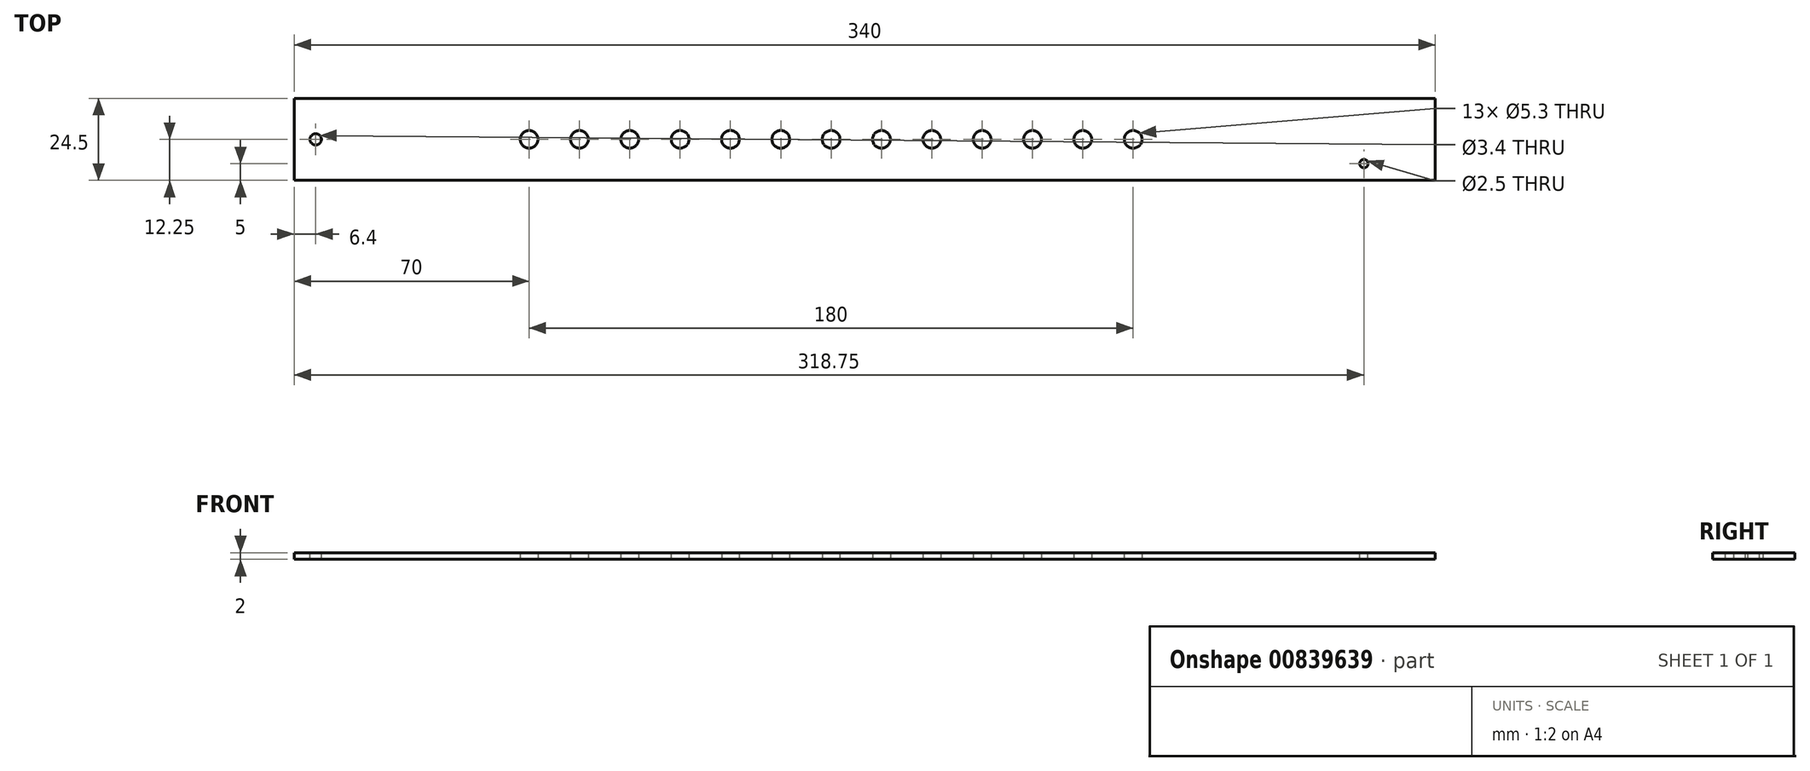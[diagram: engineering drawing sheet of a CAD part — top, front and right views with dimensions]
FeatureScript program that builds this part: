
annotation { "Feature Type Name" : "Feature", "Feature Type Description" : "" }
export const myFeature = defineFeature(function(context is Context, id is Id, definition is map)
    precondition{}
    {
        {
            var Q0;
            Q0=qCreatedBy(makeId("Top.planeOp"),FACE);
            var sketch = newSketch(context, id + "F0", { "sketchPlane" : qUnion([Q0])});
            skLineSegment(sketch, "E0.bottom", {"start": v(150, -12.25) * mm, "end": v(-150, -12.25) * mm});
            skLineSegment(sketch, "E0.top", {"start": v(150, 12.25) * mm, "end": v(-150, 12.25) * mm});
            skLineSegment(sketch, "E0.left", {"start": v(150, -12.25) * mm, "end": v(150, 12.25) * mm});
            skLineSegment(sketch, "E0.right", {"start": v(-150, -12.25) * mm, "end": v(-150, 12.25) * mm});
            skPoint(sketch, "E0.middle", {"position": v(0, 0) * mm});
            skCircle(sketch, "E1.3.0.0", {"center": v(-90, 0) * mm, "radius": 2.65 * mm});
            skCircle(sketch, "E1.4.0.0", {"center": v(-75, 0) * mm, "radius": 2.65 * mm});
            skCircle(sketch, "E1.5.0.0", {"center": v(-60, 0) * mm, "radius": 2.65 * mm});
            skCircle(sketch, "E1.6.0.0", {"center": v(-45, 0) * mm, "radius": 2.65 * mm});
            skCircle(sketch, "E1.7.0.0", {"center": v(-30, 0) * mm, "radius": 2.65 * mm});
            skCircle(sketch, "E1.8.0.0", {"center": v(-15, 0) * mm, "radius": 2.65 * mm});
            skCircle(sketch, "E1.9.0.0", {"center": v(0, 0) * mm, "radius": 2.65 * mm});
            skCircle(sketch, "E1.10.0.0", {"center": v(15, 0) * mm, "radius": 2.65 * mm});
            skCircle(sketch, "E1.11.0.0", {"center": v(30, 0) * mm, "radius": 2.65 * mm});
            skCircle(sketch, "E1.12.0.0", {"center": v(45, 0) * mm, "radius": 2.65 * mm});
            skCircle(sketch, "E1.13.0.0", {"center": v(60, 0) * mm, "radius": 2.65 * mm});
            skCircle(sketch, "E1.14.0.0", {"center": v(75, 0) * mm, "radius": 2.65 * mm});
            skCircle(sketch, "E1.15.0.0", {"center": v(90, 0) * mm, "radius": 2.65 * mm});
            skLineSegment(sketch, "E1.direction1", {"start": v(-135, 0) * mm, "end": v(-120, 0) * mm, "construction": true});
            skSolve(sketch);
        }
        {
            var Q0;
            Q0=makeQuery(id+"F0.imprint","IMPRINT",FACE,{"disambiguationData":[TD([[makeQuery(id+"F0.imprint","IMPRINT",EDGE,{"derivedFrom":sQuery(id+"F0.wireOp",EDGE,"E0.bottom")}),-1.0]])]});
            extrude(context, id + "F1", {"entities" : qUnion([Q0]), "depth" : 2 * mm, "offsetDistance" : 25 * mm});
        }
        {
            var Q0;
            Q0=makeQuery(id+"F1.opExtrude","SWEPT_FACE",FACE,{"disambiguationData":[OSD([sQuery(id+"F0.wireOp",EDGE,"E0.right")])]});
            extrude(context, id + "F2", {"entities" : qUnion([Q0]), "operationType" : NewBodyOperationType.ADD, "depth" : 10 * mm, "offsetDistance" : 25 * mm});
        }
        {
            var Q0;
            Q0=makeQuery(id+"F1.opExtrude","SWEPT_FACE",FACE,{"disambiguationData":[OSD([sQuery(id+"F0.wireOp",EDGE,"E0.left")])]});
            extrude(context, id + "F3", {"entities" : qUnion([Q0]), "operationType" : NewBodyOperationType.ADD, "depth" : 30 * mm, "offsetDistance" : 25 * mm});
        }
        {
            var Q0;
            {var subQ0=sQuery(id+"F0.wireOp",EDGE,"E0.left");var subQ1=sQuery(id+"F0.wireOp",EDGE,"E0.right");Q0=makeQuery(id+"F3.boolean.opBoolean","MERGE",FACE,{"derivedFrom":[makeQuery(id+"F2.boolean.opBoolean","MERGE",FACE,{"derivedFrom":[makeQuery(id+"F1.opExtrude","CAP_FACE",FACE,{"disambiguationData":[OSD([sQuery(id+"F0.wireOp",EDGE,"E0.bottom"),sQuery(id+"F0.wireOp",EDGE,"E0.top"),subQ0,subQ1,sQuery(id+"F0.wireOp",EDGE,"LckrCdrf-Oz9b-iWqB-HkfW-gHpTPrbceAxr"),sQuery(id+"F0.wireOp",EDGE,"E1.1.0.0"),sQuery(id+"F0.wireOp",EDGE,"E1.2.0.0"),sQuery(id+"F0.wireOp",EDGE,"E1.3.0.0"),sQuery(id+"F0.wireOp",EDGE,"E1.4.0.0"),sQuery(id+"F0.wireOp",EDGE,"E1.5.0.0"),sQuery(id+"F0.wireOp",EDGE,"E1.6.0.0"),sQuery(id+"F0.wireOp",EDGE,"E1.7.0.0"),sQuery(id+"F0.wireOp",EDGE,"E1.8.0.0"),sQuery(id+"F0.wireOp",EDGE,"E1.9.0.0"),sQuery(id+"F0.wireOp",EDGE,"E1.10.0.0"),sQuery(id+"F0.wireOp",EDGE,"E1.11.0.0"),sQuery(id+"F0.wireOp",EDGE,"E1.12.0.0"),sQuery(id+"F0.wireOp",EDGE,"E1.13.0.0"),sQuery(id+"F0.wireOp",EDGE,"E1.14.0.0"),sQuery(id+"F0.wireOp",EDGE,"E1.15.0.0"),sQuery(id+"F0.wireOp",EDGE,"E1.16.0.0"),sQuery(id+"F0.wireOp",EDGE,"E1.17.0.0"),sQuery(id+"F0.wireOp",EDGE,"E1.18.0.0")])],"isStart":false}),makeQuery(id+"F2.opExtrude","SWEPT_FACE",FACE,{"disambiguationData":[OSD([subQ1]),TDD([makeQuery(id+"F1.opExtrude","CAP_EDGE",EDGE,{"disambiguationData":[OSD([subQ1])],"isStart":false})])]})]}),makeQuery(id+"F3.opExtrude","SWEPT_FACE",FACE,{"disambiguationData":[OSD([subQ0]),TDD([makeQuery(id+"F1.opExtrude","CAP_EDGE",EDGE,{"disambiguationData":[OSD([subQ0])],"isStart":false})])]})]});}
            var sketch = newSketch(context, id + "F4", { "sketchPlane" : qUnion([Q0])});
            skCircle(sketch, "E2", {"center": v(-153.6, 0) * mm, "radius": 1.7 * mm});
            skSolve(sketch);
        }
        {
            var Q0;
            Q0=makeQuery(id+"F4.imprint","IMPRINT",FACE,{"disambiguationData":[TD([[makeQuery(id+"F4.imprint","IMPRINT",EDGE,{"derivedFrom":sQuery(id+"F4.wireOp",EDGE,"E2")}),1.0]])]});
            extrude(context, id + "F5", {"entities" : qUnion([Q0]), "operationType" : NewBodyOperationType.REMOVE, "endBound" : BoundingType.UP_TO_NEXT, "oppositeDirection" : true, "depth" : 25 * mm, "offsetDistance" : 25 * mm});
        }
        {
            var Q0;
            {var subQ0=sQuery(id+"F0.wireOp",EDGE,"E0.left");var subQ1=sQuery(id+"F0.wireOp",EDGE,"E0.right");Q0=makeQuery(id+"F3.boolean.opBoolean","MERGE",FACE,{"derivedFrom":[makeQuery(id+"F2.boolean.opBoolean","MERGE",FACE,{"derivedFrom":[makeQuery(id+"F1.opExtrude","CAP_FACE",FACE,{"disambiguationData":[OSD([sQuery(id+"F0.wireOp",EDGE,"E0.bottom"),sQuery(id+"F0.wireOp",EDGE,"E0.top"),subQ0,subQ1,sQuery(id+"F0.wireOp",EDGE,"LckrCdrf-Oz9b-iWqB-HkfW-gHpTPrbceAxr"),sQuery(id+"F0.wireOp",EDGE,"E1.1.0.0"),sQuery(id+"F0.wireOp",EDGE,"E1.2.0.0"),sQuery(id+"F0.wireOp",EDGE,"E1.3.0.0"),sQuery(id+"F0.wireOp",EDGE,"E1.4.0.0"),sQuery(id+"F0.wireOp",EDGE,"E1.5.0.0"),sQuery(id+"F0.wireOp",EDGE,"E1.6.0.0"),sQuery(id+"F0.wireOp",EDGE,"E1.7.0.0"),sQuery(id+"F0.wireOp",EDGE,"E1.8.0.0"),sQuery(id+"F0.wireOp",EDGE,"E1.9.0.0"),sQuery(id+"F0.wireOp",EDGE,"E1.10.0.0"),sQuery(id+"F0.wireOp",EDGE,"E1.11.0.0"),sQuery(id+"F0.wireOp",EDGE,"E1.12.0.0"),sQuery(id+"F0.wireOp",EDGE,"E1.13.0.0"),sQuery(id+"F0.wireOp",EDGE,"E1.14.0.0"),sQuery(id+"F0.wireOp",EDGE,"E1.15.0.0"),sQuery(id+"F0.wireOp",EDGE,"E1.16.0.0"),sQuery(id+"F0.wireOp",EDGE,"E1.17.0.0"),sQuery(id+"F0.wireOp",EDGE,"E1.18.0.0")])],"isStart":false}),makeQuery(id+"F2.opExtrude","SWEPT_FACE",FACE,{"disambiguationData":[OSD([subQ1]),TDD([makeQuery(id+"F1.opExtrude","CAP_EDGE",EDGE,{"disambiguationData":[OSD([subQ1])],"isStart":false})])]})]}),makeQuery(id+"F3.opExtrude","SWEPT_FACE",FACE,{"disambiguationData":[OSD([subQ0]),TDD([makeQuery(id+"F1.opExtrude","CAP_EDGE",EDGE,{"disambiguationData":[OSD([subQ0])],"isStart":false})])]})]});}
            var sketch = newSketch(context, id + "F6", { "sketchPlane" : qUnion([Q0])});
            skCircle(sketch, "E3", {"center": v(158.75, -7.25) * mm, "radius": 1.25 * mm});
            skSolve(sketch);
        }
        {
            var Q0;
            Q0=makeQuery(id+"F6.imprint","IMPRINT",FACE,{"disambiguationData":[TD([[makeQuery(id+"F6.imprint","IMPRINT",EDGE,{"derivedFrom":sQuery(id+"F6.wireOp",EDGE,"E3")}),1.0]])]});
            extrude(context, id + "F7", {"entities" : qUnion([Q0]), "operationType" : NewBodyOperationType.REMOVE, "endBound" : BoundingType.UP_TO_NEXT, "oppositeDirection" : true, "depth" : 25 * mm, "offsetDistance" : 25 * mm});
        }
    });
